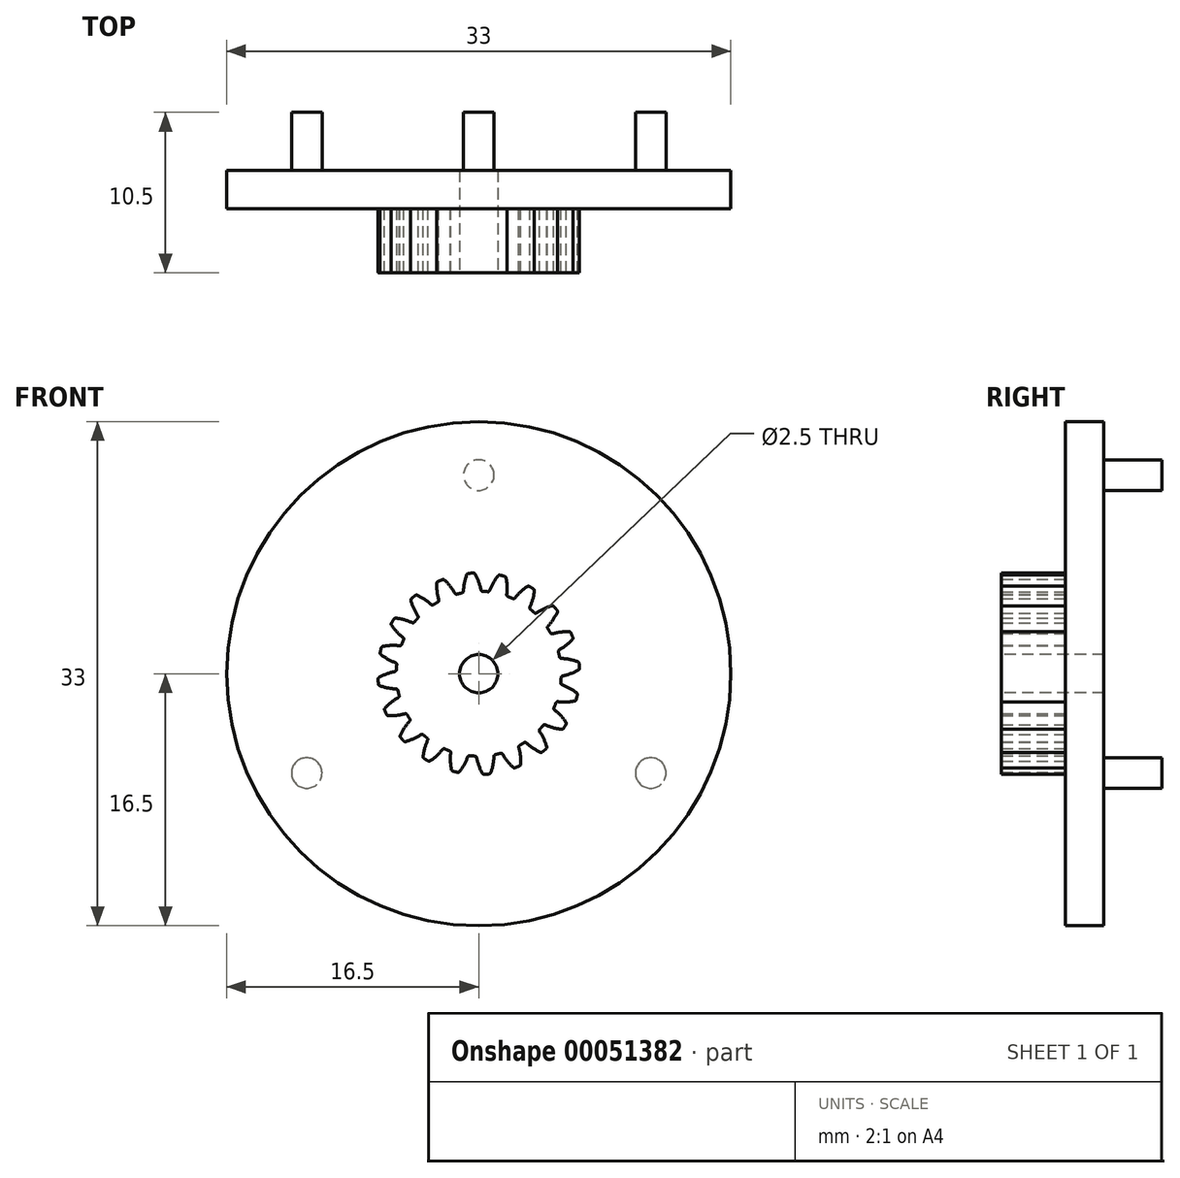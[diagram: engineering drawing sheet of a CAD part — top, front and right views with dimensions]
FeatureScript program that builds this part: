
annotation { "Feature Type Name" : "Feature", "Feature Type Description" : "" }
export const myFeature = defineFeature(function(context is Context, id is Id, definition is map)
    precondition{}
    {
        {
            var Q0;
            Q0=qCreatedBy(makeId("Front.planeOp"),FACE);
            var sketch = newSketch(context, id + "F0", { "sketchPlane" : qUnion([Q0])});
            skCircle(sketch, "E0", {"center": v(0, 0) * mm, "radius": 6 * mm, "construction": true});
            skCircle(sketch, "E1", {"center": v(0, 0) * mm, "radius": 5.4 * mm, "construction": true});
            skCircle(sketch, "E2", {"center": v(0, 0) * mm, "radius": 6.6 * mm, "construction": true});
            skLineSegment(sketch, "E3", {"start": v(0, 0) * mm, "end": v(0, 7.77) * mm, "construction": true});
            skPoint(sketch, "E4", {"position": v(0, 6) * mm});
            skLineSegment(sketch, "E5", {"start": v(0, 6) * mm, "end": v(-7.8, 6) * mm, "construction": true});
            skCircle(sketch, "E6.cCircle", {"center": v(0, 0) * mm, "radius": 7.77 * mm, "construction": true});
            skLineSegment(sketch, "E6.0", {"start": v(-0.61, 7.77) * mm, "end": v(0.61, 7.77) * mm, "construction": true});
            skLineSegment(sketch, "E6.1", {"start": v(0.61, 7.77) * mm, "end": v(1.82, 7.58) * mm, "construction": true});
            skLineSegment(sketch, "E6.2", {"start": v(1.82, 7.58) * mm, "end": v(2.98, 7.2) * mm, "construction": true});
            skLineSegment(sketch, "E6.3", {"start": v(2.98, 7.2) * mm, "end": v(4.07, 6.65) * mm, "construction": true});
            skLineSegment(sketch, "E6.4", {"start": v(4.07, 6.65) * mm, "end": v(5.06, 5.93) * mm, "construction": true});
            skLineSegment(sketch, "E6.5", {"start": v(5.06, 5.93) * mm, "end": v(5.93, 5.06) * mm, "construction": true});
            skLineSegment(sketch, "E6.6", {"start": v(5.93, 5.06) * mm, "end": v(6.65, 4.07) * mm, "construction": true});
            skLineSegment(sketch, "E6.7", {"start": v(6.65, 4.07) * mm, "end": v(7.2, 2.98) * mm, "construction": true});
            skLineSegment(sketch, "E6.8", {"start": v(7.2, 2.98) * mm, "end": v(7.58, 1.82) * mm, "construction": true});
            skLineSegment(sketch, "E6.9", {"start": v(7.58, 1.82) * mm, "end": v(7.77, 0.61) * mm, "construction": true});
            skLineSegment(sketch, "E6.10", {"start": v(7.77, 0.61) * mm, "end": v(7.77, -0.61) * mm, "construction": true});
            skLineSegment(sketch, "E6.11", {"start": v(7.77, -0.61) * mm, "end": v(7.58, -1.82) * mm, "construction": true});
            skLineSegment(sketch, "E6.12", {"start": v(7.58, -1.82) * mm, "end": v(7.2, -2.98) * mm, "construction": true});
            skLineSegment(sketch, "E6.13", {"start": v(7.2, -2.98) * mm, "end": v(6.65, -4.07) * mm, "construction": true});
            skLineSegment(sketch, "E6.14", {"start": v(6.65, -4.07) * mm, "end": v(5.93, -5.06) * mm, "construction": true});
            skLineSegment(sketch, "E6.15", {"start": v(5.93, -5.06) * mm, "end": v(5.06, -5.93) * mm, "construction": true});
            skLineSegment(sketch, "E6.16", {"start": v(5.06, -5.93) * mm, "end": v(4.07, -6.65) * mm, "construction": true});
            skLineSegment(sketch, "E6.17", {"start": v(4.07, -6.65) * mm, "end": v(2.98, -7.2) * mm, "construction": true});
            skLineSegment(sketch, "E6.18", {"start": v(2.98, -7.2) * mm, "end": v(1.82, -7.58) * mm, "construction": true});
            skLineSegment(sketch, "E6.19", {"start": v(1.82, -7.58) * mm, "end": v(0.61, -7.77) * mm, "construction": true});
            skLineSegment(sketch, "E6.20", {"start": v(0.61, -7.77) * mm, "end": v(-0.61, -7.77) * mm, "construction": true});
            skLineSegment(sketch, "E6.21", {"start": v(-0.61, -7.77) * mm, "end": v(-1.82, -7.58) * mm, "construction": true});
            skLineSegment(sketch, "E6.22", {"start": v(-1.82, -7.58) * mm, "end": v(-2.98, -7.2) * mm, "construction": true});
            skLineSegment(sketch, "E6.23", {"start": v(-2.98, -7.2) * mm, "end": v(-4.07, -6.65) * mm, "construction": true});
            skLineSegment(sketch, "E6.24", {"start": v(-4.07, -6.65) * mm, "end": v(-5.06, -5.93) * mm, "construction": true});
            skLineSegment(sketch, "E6.25", {"start": v(-5.06, -5.93) * mm, "end": v(-5.93, -5.06) * mm, "construction": true});
            skLineSegment(sketch, "E6.26", {"start": v(-5.93, -5.06) * mm, "end": v(-6.65, -4.07) * mm, "construction": true});
            skLineSegment(sketch, "E6.27", {"start": v(-6.65, -4.07) * mm, "end": v(-7.2, -2.98) * mm, "construction": true});
            skLineSegment(sketch, "E6.28", {"start": v(-7.2, -2.98) * mm, "end": v(-7.58, -1.82) * mm, "construction": true});
            skLineSegment(sketch, "E6.29", {"start": v(-7.58, -1.82) * mm, "end": v(-7.77, -0.61) * mm, "construction": true});
            skLineSegment(sketch, "E6.30", {"start": v(-7.77, -0.61) * mm, "end": v(-7.77, 0.61) * mm, "construction": true});
            skLineSegment(sketch, "E6.31", {"start": v(-7.77, 0.61) * mm, "end": v(-7.58, 1.82) * mm, "construction": true});
            skLineSegment(sketch, "E6.32", {"start": v(-7.58, 1.82) * mm, "end": v(-7.2, 2.98) * mm, "construction": true});
            skLineSegment(sketch, "E6.33", {"start": v(-7.2, 2.98) * mm, "end": v(-6.65, 4.07) * mm, "construction": true});
            skLineSegment(sketch, "E6.34", {"start": v(-6.65, 4.07) * mm, "end": v(-5.93, 5.06) * mm, "construction": true});
            skLineSegment(sketch, "E6.35", {"start": v(-5.93, 5.06) * mm, "end": v(-5.06, 5.93) * mm, "construction": true});
            skLineSegment(sketch, "E6.36", {"start": v(-5.06, 5.93) * mm, "end": v(-4.07, 6.65) * mm, "construction": true});
            skLineSegment(sketch, "E6.37", {"start": v(-4.07, 6.65) * mm, "end": v(-2.98, 7.2) * mm, "construction": true});
            skLineSegment(sketch, "E6.38", {"start": v(-2.98, 7.2) * mm, "end": v(-1.82, 7.58) * mm, "construction": true});
            skLineSegment(sketch, "E6.39", {"start": v(-1.82, 7.58) * mm, "end": v(-0.61, 7.77) * mm, "construction": true});
            skPoint(sketch, "E6.0.midPoint", {"position": v(0, 7.77) * mm});
            skLineSegment(sketch, "E7.0", {"start": v(0, 7.77) * mm, "end": v(1.22, 7.68) * mm, "construction": true});
            skLineSegment(sketch, "E7.1", {"start": v(1.22, 7.68) * mm, "end": v(2.4, 7.4) * mm, "construction": true});
            skLineSegment(sketch, "E7.2", {"start": v(2.4, 7.4) * mm, "end": v(3.53, 6.93) * mm, "construction": true});
            skLineSegment(sketch, "E7.3", {"start": v(3.53, 6.93) * mm, "end": v(4.57, 6.29) * mm, "construction": true});
            skLineSegment(sketch, "E7.4", {"start": v(4.57, 6.29) * mm, "end": v(5.5, 5.5) * mm, "construction": true});
            skLineSegment(sketch, "E7.5", {"start": v(5.5, 5.5) * mm, "end": v(6.29, 4.57) * mm, "construction": true});
            skLineSegment(sketch, "E7.6", {"start": v(6.29, 4.57) * mm, "end": v(6.93, 3.53) * mm, "construction": true});
            skLineSegment(sketch, "E7.7", {"start": v(6.93, 3.53) * mm, "end": v(7.4, 2.4) * mm, "construction": true});
            skLineSegment(sketch, "E7.8", {"start": v(7.4, 2.4) * mm, "end": v(7.68, 1.22) * mm, "construction": true});
            skLineSegment(sketch, "E7.9", {"start": v(7.68, 1.22) * mm, "end": v(7.77, 0) * mm, "construction": true});
            skLineSegment(sketch, "E7.10", {"start": v(7.77, 0) * mm, "end": v(7.68, -1.22) * mm, "construction": true});
            skLineSegment(sketch, "E7.11", {"start": v(7.68, -1.22) * mm, "end": v(7.4, -2.4) * mm, "construction": true});
            skLineSegment(sketch, "E7.12", {"start": v(7.4, -2.4) * mm, "end": v(6.93, -3.53) * mm, "construction": true});
            skLineSegment(sketch, "E7.13", {"start": v(6.93, -3.53) * mm, "end": v(6.29, -4.57) * mm, "construction": true});
            skLineSegment(sketch, "E7.14", {"start": v(6.29, -4.57) * mm, "end": v(5.5, -5.5) * mm, "construction": true});
            skLineSegment(sketch, "E7.15", {"start": v(5.5, -5.5) * mm, "end": v(4.57, -6.29) * mm, "construction": true});
            skLineSegment(sketch, "E7.16", {"start": v(4.57, -6.29) * mm, "end": v(3.53, -6.93) * mm, "construction": true});
            skLineSegment(sketch, "E7.17", {"start": v(3.53, -6.93) * mm, "end": v(2.4, -7.4) * mm, "construction": true});
            skLineSegment(sketch, "E7.18", {"start": v(2.4, -7.4) * mm, "end": v(1.22, -7.68) * mm, "construction": true});
            skLineSegment(sketch, "E7.19", {"start": v(1.22, -7.68) * mm, "end": v(0, -7.77) * mm, "construction": true});
            skLineSegment(sketch, "E7.20", {"start": v(0, -7.77) * mm, "end": v(-1.22, -7.68) * mm, "construction": true});
            skLineSegment(sketch, "E7.21", {"start": v(-1.22, -7.68) * mm, "end": v(-2.4, -7.4) * mm, "construction": true});
            skLineSegment(sketch, "E7.22", {"start": v(-2.4, -7.4) * mm, "end": v(-3.53, -6.93) * mm, "construction": true});
            skLineSegment(sketch, "E7.23", {"start": v(-3.53, -6.93) * mm, "end": v(-4.57, -6.29) * mm, "construction": true});
            skLineSegment(sketch, "E7.24", {"start": v(-4.57, -6.29) * mm, "end": v(-5.5, -5.5) * mm, "construction": true});
            skLineSegment(sketch, "E7.25", {"start": v(-5.5, -5.5) * mm, "end": v(-6.29, -4.57) * mm, "construction": true});
            skLineSegment(sketch, "E7.26", {"start": v(-6.29, -4.57) * mm, "end": v(-6.93, -3.53) * mm, "construction": true});
            skLineSegment(sketch, "E7.27", {"start": v(-6.93, -3.53) * mm, "end": v(-7.4, -2.4) * mm, "construction": true});
            skLineSegment(sketch, "E7.28", {"start": v(-7.4, -2.4) * mm, "end": v(-7.68, -1.22) * mm, "construction": true});
            skLineSegment(sketch, "E7.29", {"start": v(-7.68, -1.22) * mm, "end": v(-7.77, 0) * mm, "construction": true});
            skLineSegment(sketch, "E7.30", {"start": v(-7.77, 0) * mm, "end": v(-7.68, 1.22) * mm, "construction": true});
            skLineSegment(sketch, "E7.31", {"start": v(-7.68, 1.22) * mm, "end": v(-7.4, 2.4) * mm, "construction": true});
            skLineSegment(sketch, "E7.32", {"start": v(-7.4, 2.4) * mm, "end": v(-6.93, 3.53) * mm, "construction": true});
            skLineSegment(sketch, "E7.33", {"start": v(-6.93, 3.53) * mm, "end": v(-6.29, 4.57) * mm, "construction": true});
            skLineSegment(sketch, "E7.34", {"start": v(-6.29, 4.57) * mm, "end": v(-5.5, 5.5) * mm, "construction": true});
            skLineSegment(sketch, "E7.35", {"start": v(-5.5, 5.5) * mm, "end": v(-4.57, 6.29) * mm, "construction": true});
            skLineSegment(sketch, "E7.36", {"start": v(-4.57, 6.29) * mm, "end": v(-3.53, 6.93) * mm, "construction": true});
            skLineSegment(sketch, "E7.37", {"start": v(-3.53, 6.93) * mm, "end": v(-2.4, 7.4) * mm, "construction": true});
            skLineSegment(sketch, "E7.38", {"start": v(-2.4, 7.4) * mm, "end": v(-1.22, 7.68) * mm, "construction": true});
            skLineSegment(sketch, "E7.39", {"start": v(-1.22, 7.68) * mm, "end": v(0, 7.77) * mm, "construction": true});
            skLineSegment(sketch, "E8", {"start": v(0, 0) * mm, "end": v(-0.61, 7.77) * mm, "construction": true});
            skLineSegment(sketch, "E9", {"start": v(0, 6) * mm, "end": v(-7.35, 3.32) * mm, "construction": true});
            skCircle(sketch, "E10", {"center": v(0, 6) * mm, "radius": 3.6 * mm, "construction": true});
            skPoint(sketch, "E11", {"position": v(-3.38, 4.77) * mm});
            skCircle(sketch, "E12", {"center": v(-3.38, 4.77) * mm, "radius": 3.6 * mm, "construction": true});
            skArc(sketch, "E13", {"start": v(-0.24, 6.53) * mm, "mid": v(0, 6.02) * mm, "end": v(0.14, 5.49) * mm});
            skArc(sketch, "E14.MirrorCS", {"start": v(-0.78, 6.49) * mm, "mid": v(-0.93, 5.95) * mm, "end": v(-1, 5.4) * mm});
            skArc(sketch, "E15", {"start": v(-0.68, 6.56) * mm, "mid": v(-0.52, 6.58) * mm, "end": v(-0.35, 6.6) * mm});
            skArc(sketch, "E16", {"start": v(-1.1, 5.29) * mm, "mid": v(0.42, -5.38) * mm, "end": v(0.26, 5.4) * mm});
            skPoint(sketch, "E17.visualSharp", {"position": v(-1, 5.3) * mm});
            skArc(sketch, "E17.filletArc", {"start": v(-1.1, 5.29) * mm, "mid": v(-1.03, 5.33) * mm, "end": v(-1, 5.4) * mm});
            skPoint(sketch, "E18.visualSharp", {"position": v(0.16, 5.4) * mm});
            skArc(sketch, "E18.filletArc", {"start": v(0.14, 5.49) * mm, "mid": v(0.18, 5.42) * mm, "end": v(0.26, 5.4) * mm});
            skPoint(sketch, "E19.visualSharp", {"position": v(-0.76, 6.56) * mm});
            skArc(sketch, "E19.filletArc", {"start": v(-0.68, 6.56) * mm, "mid": v(-0.74, 6.54) * mm, "end": v(-0.78, 6.49) * mm});
            skPoint(sketch, "E20.visualSharp", {"position": v(-0.28, 6.6) * mm});
            skArc(sketch, "E20.filletArc", {"start": v(-0.24, 6.53) * mm, "mid": v(-0.29, 6.58) * mm, "end": v(-0.35, 6.6) * mm});
            skLineSegment(sketch, "E21", {"start": v(0, 0) * mm, "end": v(-1.44, 6.92) * mm, "construction": true});
            skPoint(sketch, "E22.1.0", {"position": v(-1.51, 5.18) * mm});
            skPoint(sketch, "E22.1.1", {"position": v(-1.85, 5.7) * mm});
            skArc(sketch, "E22.1.2", {"start": v(-2.25, 6.13) * mm, "mid": v(-1.87, 5.73) * mm, "end": v(-1.56, 5.27) * mm});
            skArc(sketch, "E22.1.3", {"start": v(-2.68, 6.03) * mm, "mid": v(-2.53, 6.1) * mm, "end": v(-2.37, 6.16) * mm});
            skPoint(sketch, "E22.1.4", {"position": v(-2.3, 6.18) * mm});
            skPoint(sketch, "E22.1.5", {"position": v(-2.6, 4.74) * mm});
            skArc(sketch, "E22.1.6", {"start": v(-2.75, 5.93) * mm, "mid": v(-2.73, 5.37) * mm, "end": v(-2.62, 4.83) * mm});
            skPoint(sketch, "E22.1.7", {"position": v(-2.74, 6) * mm});
            skArc(sketch, "E22.1.8", {"start": v(-1.56, 5.27) * mm, "mid": v(-1.5, 5.21) * mm, "end": v(-1.42, 5.2) * mm});
            skArc(sketch, "E22.1.9", {"start": v(-2.68, 6.03) * mm, "mid": v(-2.73, 6) * mm, "end": v(-2.75, 5.93) * mm});
            skArc(sketch, "E22.1.10", {"start": v(-2.68, 4.69) * mm, "mid": v(-2.63, 4.75) * mm, "end": v(-2.62, 4.83) * mm});
            skArc(sketch, "E22.1.11", {"start": v(-2.25, 6.13) * mm, "mid": v(-2.3, 6.16) * mm, "end": v(-2.37, 6.16) * mm});
            skPoint(sketch, "E22.2.0", {"position": v(-3.04, 4.46) * mm});
            skPoint(sketch, "E22.2.1", {"position": v(-3.53, 4.85) * mm});
            skArc(sketch, "E22.2.2", {"start": v(-4.03, 5.14) * mm, "mid": v(-3.55, 4.87) * mm, "end": v(-3.11, 4.53) * mm});
            skArc(sketch, "E22.2.3", {"start": v(-4.4, 4.91) * mm, "mid": v(-4.29, 5.02) * mm, "end": v(-4.16, 5.12) * mm});
            skPoint(sketch, "E22.2.4", {"position": v(-4.1, 5.17) * mm});
            skPoint(sketch, "E22.2.5", {"position": v(-3.93, 3.7) * mm});
            skArc(sketch, "E22.2.6", {"start": v(-4.45, 4.79) * mm, "mid": v(-4.25, 4.27) * mm, "end": v(-3.98, 3.78) * mm});
            skPoint(sketch, "E22.2.7", {"position": v(-4.46, 4.86) * mm});
            skArc(sketch, "E22.2.8", {"start": v(-3.11, 4.53) * mm, "mid": v(-3.04, 4.5) * mm, "end": v(-2.96, 4.51) * mm});
            skArc(sketch, "E22.2.9", {"start": v(-4.4, 4.91) * mm, "mid": v(-4.45, 4.85) * mm, "end": v(-4.45, 4.79) * mm});
            skArc(sketch, "E22.2.10", {"start": v(-4, 3.63) * mm, "mid": v(-3.96, 3.7) * mm, "end": v(-3.98, 3.78) * mm});
            skArc(sketch, "E22.2.11", {"start": v(-4.03, 5.14) * mm, "mid": v(-4.1, 5.15) * mm, "end": v(-4.16, 5.12) * mm});
            skPoint(sketch, "E22.3.0", {"position": v(-4.27, 3.3) * mm});
            skPoint(sketch, "E22.3.1", {"position": v(-4.85, 3.53) * mm});
            skArc(sketch, "E22.3.2", {"start": v(-5.43, 3.64) * mm, "mid": v(-4.88, 3.53) * mm, "end": v(-4.36, 3.34) * mm});
            skArc(sketch, "E22.3.3", {"start": v(-5.71, 3.3) * mm, "mid": v(-5.63, 3.45) * mm, "end": v(-5.54, 3.59) * mm});
            skPoint(sketch, "E22.3.4", {"position": v(-5.5, 3.65) * mm});
            skPoint(sketch, "E22.3.5", {"position": v(-4.88, 2.3) * mm});
            skArc(sketch, "E22.3.6", {"start": v(-5.7, 3.18) * mm, "mid": v(-5.36, 2.74) * mm, "end": v(-4.96, 2.36) * mm});
            skPoint(sketch, "E22.3.7", {"position": v(-5.75, 3.24) * mm});
            skArc(sketch, "E22.3.8", {"start": v(-4.36, 3.34) * mm, "mid": v(-4.28, 3.34) * mm, "end": v(-4.21, 3.38) * mm});
            skArc(sketch, "E22.3.9", {"start": v(-5.71, 3.3) * mm, "mid": v(-5.73, 3.24) * mm, "end": v(-5.7, 3.18) * mm});
            skArc(sketch, "E22.3.10", {"start": v(-4.92, 2.22) * mm, "mid": v(-4.92, 2.3) * mm, "end": v(-4.96, 2.36) * mm});
            skArc(sketch, "E22.3.11", {"start": v(-5.43, 3.64) * mm, "mid": v(-5.5, 3.63) * mm, "end": v(-5.54, 3.59) * mm});
            skPoint(sketch, "E22.4.0", {"position": v(-5.08, 1.82) * mm});
            skPoint(sketch, "E22.4.1", {"position": v(-5.7, 1.85) * mm});
            skArc(sketch, "E22.4.2", {"start": v(-6.28, 1.79) * mm, "mid": v(-5.73, 1.85) * mm, "end": v(-5.18, 1.83) * mm});
            skArc(sketch, "E22.4.3", {"start": v(-6.45, 1.38) * mm, "mid": v(-6.42, 1.54) * mm, "end": v(-6.38, 1.7) * mm});
            skPoint(sketch, "E22.4.4", {"position": v(-6.36, 1.77) * mm});
            skPoint(sketch, "E22.4.5", {"position": v(-5.36, 0.68) * mm});
            skArc(sketch, "E22.4.6", {"start": v(-6.41, 1.26) * mm, "mid": v(-5.95, 0.95) * mm, "end": v(-5.44, 0.72) * mm});
            skPoint(sketch, "E22.4.7", {"position": v(-6.47, 1.3) * mm});
            skArc(sketch, "E22.4.8", {"start": v(-5.18, 1.83) * mm, "mid": v(-5.1, 1.85) * mm, "end": v(-5.05, 1.91) * mm});
            skArc(sketch, "E22.4.9", {"start": v(-6.45, 1.38) * mm, "mid": v(-6.45, 1.31) * mm, "end": v(-6.41, 1.26) * mm});
            skArc(sketch, "E22.4.10", {"start": v(-5.37, 0.6) * mm, "mid": v(-5.38, 0.67) * mm, "end": v(-5.44, 0.72) * mm});
            skArc(sketch, "E22.4.11", {"start": v(-6.28, 1.79) * mm, "mid": v(-6.34, 1.76) * mm, "end": v(-6.38, 1.7) * mm});
            skPoint(sketch, "E22.5.0", {"position": v(-5.4, 0.16) * mm});
            skPoint(sketch, "E22.5.1", {"position": v(-6, 0) * mm});
            skArc(sketch, "E22.5.2", {"start": v(-6.53, -0.24) * mm, "mid": v(-6.02, 0) * mm, "end": v(-5.49, 0.14) * mm});
            skArc(sketch, "E22.5.3", {"start": v(-6.56, -0.68) * mm, "mid": v(-6.58, -0.52) * mm, "end": v(-6.6, -0.35) * mm});
            skPoint(sketch, "E22.5.4", {"position": v(-6.6, -0.28) * mm});
            skPoint(sketch, "E22.5.5", {"position": v(-5.3, -1) * mm});
            skArc(sketch, "E22.5.6", {"start": v(-6.49, -0.78) * mm, "mid": v(-5.95, -0.93) * mm, "end": v(-5.4, -1) * mm});
            skPoint(sketch, "E22.5.7", {"position": v(-6.56, -0.76) * mm});
            skArc(sketch, "E22.5.8", {"start": v(-5.49, 0.14) * mm, "mid": v(-5.42, 0.18) * mm, "end": v(-5.4, 0.26) * mm});
            skArc(sketch, "E22.5.9", {"start": v(-6.56, -0.68) * mm, "mid": v(-6.54, -0.74) * mm, "end": v(-6.49, -0.78) * mm});
            skArc(sketch, "E22.5.10", {"start": v(-5.29, -1.1) * mm, "mid": v(-5.33, -1.03) * mm, "end": v(-5.4, -1) * mm});
            skArc(sketch, "E22.5.11", {"start": v(-6.53, -0.24) * mm, "mid": v(-6.58, -0.29) * mm, "end": v(-6.6, -0.35) * mm});
            skPoint(sketch, "E22.6.0", {"position": v(-5.18, -1.51) * mm});
            skPoint(sketch, "E22.6.1", {"position": v(-5.7, -1.85) * mm});
            skArc(sketch, "E22.6.2", {"start": v(-6.13, -2.25) * mm, "mid": v(-5.73, -1.87) * mm, "end": v(-5.27, -1.56) * mm});
            skArc(sketch, "E22.6.3", {"start": v(-6.03, -2.68) * mm, "mid": v(-6.1, -2.53) * mm, "end": v(-6.16, -2.37) * mm});
            skPoint(sketch, "E22.6.4", {"position": v(-6.18, -2.3) * mm});
            skPoint(sketch, "E22.6.5", {"position": v(-4.74, -2.6) * mm});
            skArc(sketch, "E22.6.6", {"start": v(-5.93, -2.75) * mm, "mid": v(-5.37, -2.73) * mm, "end": v(-4.83, -2.62) * mm});
            skPoint(sketch, "E22.6.7", {"position": v(-6, -2.74) * mm});
            skArc(sketch, "E22.6.8", {"start": v(-5.27, -1.56) * mm, "mid": v(-5.21, -1.5) * mm, "end": v(-5.2, -1.42) * mm});
            skArc(sketch, "E22.6.9", {"start": v(-6.03, -2.68) * mm, "mid": v(-6, -2.73) * mm, "end": v(-5.93, -2.75) * mm});
            skArc(sketch, "E22.6.10", {"start": v(-4.69, -2.68) * mm, "mid": v(-4.75, -2.63) * mm, "end": v(-4.83, -2.62) * mm});
            skArc(sketch, "E22.6.11", {"start": v(-6.13, -2.25) * mm, "mid": v(-6.16, -2.3) * mm, "end": v(-6.16, -2.37) * mm});
            skPoint(sketch, "E22.7.0", {"position": v(-4.46, -3.04) * mm});
            skPoint(sketch, "E22.7.1", {"position": v(-4.85, -3.53) * mm});
            skArc(sketch, "E22.7.2", {"start": v(-5.14, -4.03) * mm, "mid": v(-4.87, -3.55) * mm, "end": v(-4.53, -3.11) * mm});
            skArc(sketch, "E22.7.3", {"start": v(-4.91, -4.4) * mm, "mid": v(-5.02, -4.29) * mm, "end": v(-5.12, -4.16) * mm});
            skPoint(sketch, "E22.7.4", {"position": v(-5.17, -4.1) * mm});
            skPoint(sketch, "E22.7.5", {"position": v(-3.7, -3.93) * mm});
            skArc(sketch, "E22.7.6", {"start": v(-4.79, -4.45) * mm, "mid": v(-4.27, -4.25) * mm, "end": v(-3.78, -3.98) * mm});
            skPoint(sketch, "E22.7.7", {"position": v(-4.86, -4.46) * mm});
            skArc(sketch, "E22.7.8", {"start": v(-4.53, -3.11) * mm, "mid": v(-4.5, -3.04) * mm, "end": v(-4.51, -2.96) * mm});
            skArc(sketch, "E22.7.9", {"start": v(-4.91, -4.4) * mm, "mid": v(-4.85, -4.45) * mm, "end": v(-4.79, -4.45) * mm});
            skArc(sketch, "E22.7.10", {"start": v(-3.63, -4) * mm, "mid": v(-3.7, -3.96) * mm, "end": v(-3.78, -3.98) * mm});
            skArc(sketch, "E22.7.11", {"start": v(-5.14, -4.03) * mm, "mid": v(-5.15, -4.1) * mm, "end": v(-5.12, -4.16) * mm});
            skPoint(sketch, "E22.8.0", {"position": v(-3.3, -4.27) * mm});
            skPoint(sketch, "E22.8.1", {"position": v(-3.53, -4.85) * mm});
            skArc(sketch, "E22.8.2", {"start": v(-3.64, -5.43) * mm, "mid": v(-3.53, -4.88) * mm, "end": v(-3.34, -4.36) * mm});
            skArc(sketch, "E22.8.3", {"start": v(-3.3, -5.71) * mm, "mid": v(-3.45, -5.63) * mm, "end": v(-3.59, -5.54) * mm});
            skPoint(sketch, "E22.8.4", {"position": v(-3.65, -5.5) * mm});
            skPoint(sketch, "E22.8.5", {"position": v(-2.3, -4.88) * mm});
            skArc(sketch, "E22.8.6", {"start": v(-3.18, -5.7) * mm, "mid": v(-2.74, -5.36) * mm, "end": v(-2.36, -4.96) * mm});
            skPoint(sketch, "E22.8.7", {"position": v(-3.24, -5.75) * mm});
            skArc(sketch, "E22.8.8", {"start": v(-3.34, -4.36) * mm, "mid": v(-3.34, -4.28) * mm, "end": v(-3.38, -4.21) * mm});
            skArc(sketch, "E22.8.9", {"start": v(-3.3, -5.71) * mm, "mid": v(-3.24, -5.73) * mm, "end": v(-3.18, -5.7) * mm});
            skArc(sketch, "E22.8.10", {"start": v(-2.22, -4.92) * mm, "mid": v(-2.3, -4.92) * mm, "end": v(-2.36, -4.96) * mm});
            skArc(sketch, "E22.8.11", {"start": v(-3.64, -5.43) * mm, "mid": v(-3.63, -5.5) * mm, "end": v(-3.59, -5.54) * mm});
            skPoint(sketch, "E22.9.0", {"position": v(-1.82, -5.08) * mm});
            skPoint(sketch, "E22.9.1", {"position": v(-1.85, -5.7) * mm});
            skArc(sketch, "E22.9.2", {"start": v(-1.79, -6.28) * mm, "mid": v(-1.85, -5.73) * mm, "end": v(-1.83, -5.18) * mm});
            skArc(sketch, "E22.9.3", {"start": v(-1.38, -6.45) * mm, "mid": v(-1.54, -6.42) * mm, "end": v(-1.7, -6.38) * mm});
            skPoint(sketch, "E22.9.4", {"position": v(-1.77, -6.36) * mm});
            skPoint(sketch, "E22.9.5", {"position": v(-0.68, -5.36) * mm});
            skArc(sketch, "E22.9.6", {"start": v(-1.26, -6.41) * mm, "mid": v(-0.95, -5.95) * mm, "end": v(-0.72, -5.44) * mm});
            skPoint(sketch, "E22.9.7", {"position": v(-1.3, -6.47) * mm});
            skArc(sketch, "E22.9.8", {"start": v(-1.83, -5.18) * mm, "mid": v(-1.85, -5.1) * mm, "end": v(-1.91, -5.05) * mm});
            skArc(sketch, "E22.9.9", {"start": v(-1.38, -6.45) * mm, "mid": v(-1.31, -6.45) * mm, "end": v(-1.26, -6.41) * mm});
            skArc(sketch, "E22.9.10", {"start": v(-0.6, -5.37) * mm, "mid": v(-0.67, -5.38) * mm, "end": v(-0.72, -5.44) * mm});
            skArc(sketch, "E22.9.11", {"start": v(-1.79, -6.28) * mm, "mid": v(-1.76, -6.34) * mm, "end": v(-1.7, -6.38) * mm});
            skPoint(sketch, "E22.10.0", {"position": v(-0.16, -5.4) * mm});
            skPoint(sketch, "E22.10.1", {"position": v(0, -6) * mm});
            skArc(sketch, "E22.10.2", {"start": v(0.24, -6.53) * mm, "mid": v(0, -6.02) * mm, "end": v(-0.14, -5.49) * mm});
            skArc(sketch, "E22.10.3", {"start": v(0.68, -6.56) * mm, "mid": v(0.52, -6.58) * mm, "end": v(0.35, -6.6) * mm});
            skPoint(sketch, "E22.10.4", {"position": v(0.28, -6.6) * mm});
            skPoint(sketch, "E22.10.5", {"position": v(1, -5.3) * mm});
            skArc(sketch, "E22.10.6", {"start": v(0.78, -6.49) * mm, "mid": v(0.93, -5.95) * mm, "end": v(1, -5.4) * mm});
            skPoint(sketch, "E22.10.7", {"position": v(0.76, -6.56) * mm});
            skArc(sketch, "E22.10.8", {"start": v(-0.14, -5.49) * mm, "mid": v(-0.18, -5.42) * mm, "end": v(-0.26, -5.4) * mm});
            skArc(sketch, "E22.10.9", {"start": v(0.68, -6.56) * mm, "mid": v(0.74, -6.54) * mm, "end": v(0.78, -6.49) * mm});
            skArc(sketch, "E22.10.10", {"start": v(1.1, -5.29) * mm, "mid": v(1.03, -5.33) * mm, "end": v(1, -5.4) * mm});
            skArc(sketch, "E22.10.11", {"start": v(0.24, -6.53) * mm, "mid": v(0.29, -6.58) * mm, "end": v(0.35, -6.6) * mm});
            skPoint(sketch, "E22.11.0", {"position": v(1.51, -5.18) * mm});
            skPoint(sketch, "E22.11.1", {"position": v(1.85, -5.7) * mm});
            skArc(sketch, "E22.11.2", {"start": v(2.25, -6.13) * mm, "mid": v(1.87, -5.73) * mm, "end": v(1.56, -5.27) * mm});
            skArc(sketch, "E22.11.3", {"start": v(2.68, -6.03) * mm, "mid": v(2.53, -6.1) * mm, "end": v(2.37, -6.16) * mm});
            skPoint(sketch, "E22.11.4", {"position": v(2.3, -6.18) * mm});
            skPoint(sketch, "E22.11.5", {"position": v(2.6, -4.74) * mm});
            skArc(sketch, "E22.11.6", {"start": v(2.75, -5.93) * mm, "mid": v(2.73, -5.37) * mm, "end": v(2.62, -4.83) * mm});
            skPoint(sketch, "E22.11.7", {"position": v(2.74, -6) * mm});
            skArc(sketch, "E22.11.8", {"start": v(1.56, -5.27) * mm, "mid": v(1.5, -5.21) * mm, "end": v(1.42, -5.2) * mm});
            skArc(sketch, "E22.11.9", {"start": v(2.68, -6.03) * mm, "mid": v(2.73, -6) * mm, "end": v(2.75, -5.93) * mm});
            skArc(sketch, "E22.11.10", {"start": v(2.68, -4.69) * mm, "mid": v(2.63, -4.75) * mm, "end": v(2.62, -4.83) * mm});
            skArc(sketch, "E22.11.11", {"start": v(2.25, -6.13) * mm, "mid": v(2.3, -6.16) * mm, "end": v(2.37, -6.16) * mm});
            skPoint(sketch, "E22.12.0", {"position": v(3.04, -4.46) * mm});
            skPoint(sketch, "E22.12.1", {"position": v(3.53, -4.85) * mm});
            skArc(sketch, "E22.12.2", {"start": v(4.03, -5.14) * mm, "mid": v(3.55, -4.87) * mm, "end": v(3.11, -4.53) * mm});
            skArc(sketch, "E22.12.3", {"start": v(4.4, -4.91) * mm, "mid": v(4.29, -5.02) * mm, "end": v(4.16, -5.12) * mm});
            skPoint(sketch, "E22.12.4", {"position": v(4.1, -5.17) * mm});
            skPoint(sketch, "E22.12.5", {"position": v(3.93, -3.7) * mm});
            skArc(sketch, "E22.12.6", {"start": v(4.45, -4.79) * mm, "mid": v(4.25, -4.27) * mm, "end": v(3.98, -3.78) * mm});
            skPoint(sketch, "E22.12.7", {"position": v(4.46, -4.86) * mm});
            skArc(sketch, "E22.12.8", {"start": v(3.11, -4.53) * mm, "mid": v(3.04, -4.5) * mm, "end": v(2.96, -4.51) * mm});
            skArc(sketch, "E22.12.9", {"start": v(4.4, -4.91) * mm, "mid": v(4.45, -4.85) * mm, "end": v(4.45, -4.79) * mm});
            skArc(sketch, "E22.12.10", {"start": v(4, -3.63) * mm, "mid": v(3.96, -3.7) * mm, "end": v(3.98, -3.78) * mm});
            skArc(sketch, "E22.12.11", {"start": v(4.03, -5.14) * mm, "mid": v(4.1, -5.15) * mm, "end": v(4.16, -5.12) * mm});
            skPoint(sketch, "E22.13.0", {"position": v(4.27, -3.3) * mm});
            skPoint(sketch, "E22.13.1", {"position": v(4.85, -3.53) * mm});
            skArc(sketch, "E22.13.2", {"start": v(5.43, -3.64) * mm, "mid": v(4.88, -3.53) * mm, "end": v(4.36, -3.34) * mm});
            skArc(sketch, "E22.13.3", {"start": v(5.71, -3.3) * mm, "mid": v(5.63, -3.45) * mm, "end": v(5.54, -3.59) * mm});
            skPoint(sketch, "E22.13.4", {"position": v(5.5, -3.65) * mm});
            skPoint(sketch, "E22.13.5", {"position": v(4.88, -2.3) * mm});
            skArc(sketch, "E22.13.6", {"start": v(5.7, -3.18) * mm, "mid": v(5.36, -2.74) * mm, "end": v(4.96, -2.36) * mm});
            skPoint(sketch, "E22.13.7", {"position": v(5.75, -3.24) * mm});
            skArc(sketch, "E22.13.8", {"start": v(4.36, -3.34) * mm, "mid": v(4.28, -3.34) * mm, "end": v(4.21, -3.38) * mm});
            skArc(sketch, "E22.13.9", {"start": v(5.71, -3.3) * mm, "mid": v(5.73, -3.24) * mm, "end": v(5.7, -3.18) * mm});
            skArc(sketch, "E22.13.10", {"start": v(4.92, -2.22) * mm, "mid": v(4.92, -2.3) * mm, "end": v(4.96, -2.36) * mm});
            skArc(sketch, "E22.13.11", {"start": v(5.43, -3.64) * mm, "mid": v(5.5, -3.63) * mm, "end": v(5.54, -3.59) * mm});
            skPoint(sketch, "E22.14.0", {"position": v(5.08, -1.82) * mm});
            skPoint(sketch, "E22.14.1", {"position": v(5.7, -1.85) * mm});
            skArc(sketch, "E22.14.2", {"start": v(6.28, -1.79) * mm, "mid": v(5.73, -1.85) * mm, "end": v(5.18, -1.83) * mm});
            skArc(sketch, "E22.14.3", {"start": v(6.45, -1.38) * mm, "mid": v(6.42, -1.54) * mm, "end": v(6.38, -1.7) * mm});
            skPoint(sketch, "E22.14.4", {"position": v(6.36, -1.77) * mm});
            skPoint(sketch, "E22.14.5", {"position": v(5.36, -0.68) * mm});
            skArc(sketch, "E22.14.6", {"start": v(6.41, -1.26) * mm, "mid": v(5.95, -0.95) * mm, "end": v(5.44, -0.72) * mm});
            skPoint(sketch, "E22.14.7", {"position": v(6.47, -1.3) * mm});
            skArc(sketch, "E22.14.8", {"start": v(5.18, -1.83) * mm, "mid": v(5.1, -1.85) * mm, "end": v(5.05, -1.91) * mm});
            skArc(sketch, "E22.14.9", {"start": v(6.45, -1.38) * mm, "mid": v(6.45, -1.31) * mm, "end": v(6.41, -1.26) * mm});
            skArc(sketch, "E22.14.10", {"start": v(5.37, -0.6) * mm, "mid": v(5.38, -0.67) * mm, "end": v(5.44, -0.72) * mm});
            skArc(sketch, "E22.14.11", {"start": v(6.28, -1.79) * mm, "mid": v(6.34, -1.76) * mm, "end": v(6.38, -1.7) * mm});
            skPoint(sketch, "E22.15.0", {"position": v(5.4, -0.16) * mm});
            skPoint(sketch, "E22.15.1", {"position": v(6, 0) * mm});
            skArc(sketch, "E22.15.2", {"start": v(6.53, 0.24) * mm, "mid": v(6.02, 0) * mm, "end": v(5.49, -0.14) * mm});
            skArc(sketch, "E22.15.3", {"start": v(6.56, 0.68) * mm, "mid": v(6.58, 0.52) * mm, "end": v(6.6, 0.35) * mm});
            skPoint(sketch, "E22.15.4", {"position": v(6.6, 0.28) * mm});
            skPoint(sketch, "E22.15.5", {"position": v(5.3, 1) * mm});
            skArc(sketch, "E22.15.6", {"start": v(6.49, 0.78) * mm, "mid": v(5.95, 0.93) * mm, "end": v(5.4, 1) * mm});
            skPoint(sketch, "E22.15.7", {"position": v(6.56, 0.76) * mm});
            skArc(sketch, "E22.15.8", {"start": v(5.49, -0.14) * mm, "mid": v(5.42, -0.18) * mm, "end": v(5.4, -0.26) * mm});
            skArc(sketch, "E22.15.9", {"start": v(6.56, 0.68) * mm, "mid": v(6.54, 0.74) * mm, "end": v(6.49, 0.78) * mm});
            skArc(sketch, "E22.15.10", {"start": v(5.29, 1.1) * mm, "mid": v(5.33, 1.03) * mm, "end": v(5.4, 1) * mm});
            skArc(sketch, "E22.15.11", {"start": v(6.53, 0.24) * mm, "mid": v(6.58, 0.29) * mm, "end": v(6.6, 0.35) * mm});
            skPoint(sketch, "E22.16.0", {"position": v(5.18, 1.51) * mm});
            skPoint(sketch, "E22.16.1", {"position": v(5.7, 1.85) * mm});
            skArc(sketch, "E22.16.2", {"start": v(6.13, 2.25) * mm, "mid": v(5.73, 1.87) * mm, "end": v(5.27, 1.56) * mm});
            skArc(sketch, "E22.16.3", {"start": v(6.03, 2.68) * mm, "mid": v(6.1, 2.53) * mm, "end": v(6.16, 2.37) * mm});
            skPoint(sketch, "E22.16.4", {"position": v(6.18, 2.3) * mm});
            skPoint(sketch, "E22.16.5", {"position": v(4.74, 2.6) * mm});
            skArc(sketch, "E22.16.6", {"start": v(5.93, 2.75) * mm, "mid": v(5.37, 2.73) * mm, "end": v(4.83, 2.62) * mm});
            skPoint(sketch, "E22.16.7", {"position": v(6, 2.74) * mm});
            skArc(sketch, "E22.16.8", {"start": v(5.27, 1.56) * mm, "mid": v(5.21, 1.5) * mm, "end": v(5.2, 1.42) * mm});
            skArc(sketch, "E22.16.9", {"start": v(6.03, 2.68) * mm, "mid": v(6, 2.73) * mm, "end": v(5.93, 2.75) * mm});
            skArc(sketch, "E22.16.10", {"start": v(4.69, 2.68) * mm, "mid": v(4.75, 2.63) * mm, "end": v(4.83, 2.62) * mm});
            skArc(sketch, "E22.16.11", {"start": v(6.13, 2.25) * mm, "mid": v(6.16, 2.3) * mm, "end": v(6.16, 2.37) * mm});
            skPoint(sketch, "E22.17.0", {"position": v(4.46, 3.04) * mm});
            skPoint(sketch, "E22.17.1", {"position": v(4.85, 3.53) * mm});
            skArc(sketch, "E22.17.2", {"start": v(5.14, 4.03) * mm, "mid": v(4.87, 3.55) * mm, "end": v(4.53, 3.11) * mm});
            skArc(sketch, "E22.17.3", {"start": v(4.91, 4.4) * mm, "mid": v(5.02, 4.29) * mm, "end": v(5.12, 4.16) * mm});
            skPoint(sketch, "E22.17.4", {"position": v(5.17, 4.1) * mm});
            skPoint(sketch, "E22.17.5", {"position": v(3.7, 3.93) * mm});
            skArc(sketch, "E22.17.6", {"start": v(4.79, 4.45) * mm, "mid": v(4.27, 4.25) * mm, "end": v(3.78, 3.98) * mm});
            skPoint(sketch, "E22.17.7", {"position": v(4.86, 4.46) * mm});
            skArc(sketch, "E22.17.8", {"start": v(4.53, 3.11) * mm, "mid": v(4.5, 3.04) * mm, "end": v(4.51, 2.96) * mm});
            skArc(sketch, "E22.17.9", {"start": v(4.91, 4.4) * mm, "mid": v(4.85, 4.45) * mm, "end": v(4.79, 4.45) * mm});
            skArc(sketch, "E22.17.10", {"start": v(3.63, 4) * mm, "mid": v(3.7, 3.96) * mm, "end": v(3.78, 3.98) * mm});
            skArc(sketch, "E22.17.11", {"start": v(5.14, 4.03) * mm, "mid": v(5.15, 4.1) * mm, "end": v(5.12, 4.16) * mm});
            skPoint(sketch, "E22.18.0", {"position": v(3.3, 4.27) * mm});
            skPoint(sketch, "E22.18.1", {"position": v(3.53, 4.85) * mm});
            skArc(sketch, "E22.18.2", {"start": v(3.64, 5.43) * mm, "mid": v(3.53, 4.88) * mm, "end": v(3.34, 4.36) * mm});
            skArc(sketch, "E22.18.3", {"start": v(3.3, 5.71) * mm, "mid": v(3.45, 5.63) * mm, "end": v(3.59, 5.54) * mm});
            skPoint(sketch, "E22.18.4", {"position": v(3.65, 5.5) * mm});
            skPoint(sketch, "E22.18.5", {"position": v(2.3, 4.88) * mm});
            skArc(sketch, "E22.18.6", {"start": v(3.18, 5.7) * mm, "mid": v(2.74, 5.36) * mm, "end": v(2.36, 4.96) * mm});
            skPoint(sketch, "E22.18.7", {"position": v(3.24, 5.75) * mm});
            skArc(sketch, "E22.18.8", {"start": v(3.34, 4.36) * mm, "mid": v(3.34, 4.28) * mm, "end": v(3.38, 4.21) * mm});
            skArc(sketch, "E22.18.9", {"start": v(3.3, 5.71) * mm, "mid": v(3.24, 5.73) * mm, "end": v(3.18, 5.7) * mm});
            skArc(sketch, "E22.18.10", {"start": v(2.22, 4.92) * mm, "mid": v(2.3, 4.92) * mm, "end": v(2.36, 4.96) * mm});
            skArc(sketch, "E22.18.11", {"start": v(3.64, 5.43) * mm, "mid": v(3.63, 5.5) * mm, "end": v(3.59, 5.54) * mm});
            skPoint(sketch, "E22.19.0", {"position": v(1.82, 5.08) * mm});
            skPoint(sketch, "E22.19.1", {"position": v(1.85, 5.7) * mm});
            skArc(sketch, "E22.19.2", {"start": v(1.79, 6.28) * mm, "mid": v(1.85, 5.73) * mm, "end": v(1.83, 5.18) * mm});
            skArc(sketch, "E22.19.3", {"start": v(1.38, 6.45) * mm, "mid": v(1.54, 6.42) * mm, "end": v(1.7, 6.38) * mm});
            skPoint(sketch, "E22.19.4", {"position": v(1.77, 6.36) * mm});
            skPoint(sketch, "E22.19.5", {"position": v(0.68, 5.36) * mm});
            skArc(sketch, "E22.19.6", {"start": v(1.26, 6.41) * mm, "mid": v(0.95, 5.95) * mm, "end": v(0.72, 5.44) * mm});
            skPoint(sketch, "E22.19.7", {"position": v(1.3, 6.47) * mm});
            skArc(sketch, "E22.19.8", {"start": v(1.83, 5.18) * mm, "mid": v(1.85, 5.1) * mm, "end": v(1.91, 5.05) * mm});
            skArc(sketch, "E22.19.9", {"start": v(1.38, 6.45) * mm, "mid": v(1.31, 6.45) * mm, "end": v(1.26, 6.41) * mm});
            skArc(sketch, "E22.19.10", {"start": v(0.6, 5.37) * mm, "mid": v(0.67, 5.38) * mm, "end": v(0.72, 5.44) * mm});
            skArc(sketch, "E22.19.11", {"start": v(1.79, 6.28) * mm, "mid": v(1.76, 6.34) * mm, "end": v(1.7, 6.38) * mm});
            skSolve(sketch);
        }
        {
            var Q0;
            Q0 = qSketchRegion(id + "F0", true);
            extrude(context, id + "F1", {"entities" : qUnion([Q0]), "depth" : 4.2 * mm});
        }
        {
            var Q0;
            Q0=qCreatedBy(makeId("Front.planeOp"),FACE);
            var sketch = newSketch(context, id + "F2", { "sketchPlane" : qUnion([Q0])});
            skCircle(sketch, "E23", {"center": v(0, 0) * mm, "radius": 16.5 * mm});
            skSolve(sketch);
        }
        {
            var Q0;
            Q0 = qSketchRegion(id + "F2", true);
            extrude(context, id + "F3", {"entities" : qUnion([Q0]), "operationType" : NewBodyOperationType.ADD, "oppositeDirection" : true, "depth" : 2.5 * mm});
        }
        {
            var Q0;
            Q0=makeQuery(id+"F1.opExtrude","CAP_FACE",FACE,{"disambiguationData":[OSD([sQuery(id+"F0.wireOp",EDGE,"E13"),sQuery(id+"F0.wireOp",EDGE,"E14.MirrorCS"),sQuery(id+"F0.wireOp",EDGE,"E15"),sQuery(id+"F0.wireOp",EDGE,"E16"),sQuery(id+"F0.wireOp",EDGE,"E17.filletArc"),sQuery(id+"F0.wireOp",EDGE,"E18.filletArc"),sQuery(id+"F0.wireOp",EDGE,"E19.filletArc"),sQuery(id+"F0.wireOp",EDGE,"E20.filletArc"),sQuery(id+"F0.wireOp",EDGE,"E22.1.2"),sQuery(id+"F0.wireOp",EDGE,"E22.1.3"),sQuery(id+"F0.wireOp",EDGE,"E22.1.6"),sQuery(id+"F0.wireOp",EDGE,"E22.1.8"),sQuery(id+"F0.wireOp",EDGE,"E22.1.9"),sQuery(id+"F0.wireOp",EDGE,"E22.1.10"),sQuery(id+"F0.wireOp",EDGE,"E22.1.11"),sQuery(id+"F0.wireOp",EDGE,"E22.2.2"),sQuery(id+"F0.wireOp",EDGE,"E22.2.3"),sQuery(id+"F0.wireOp",EDGE,"E22.2.6"),sQuery(id+"F0.wireOp",EDGE,"E22.2.8"),sQuery(id+"F0.wireOp",EDGE,"E22.2.9"),sQuery(id+"F0.wireOp",EDGE,"E22.2.10"),sQuery(id+"F0.wireOp",EDGE,"E22.2.11"),sQuery(id+"F0.wireOp",EDGE,"E22.3.2"),sQuery(id+"F0.wireOp",EDGE,"E22.3.3"),sQuery(id+"F0.wireOp",EDGE,"E22.3.6"),sQuery(id+"F0.wireOp",EDGE,"E22.3.8"),sQuery(id+"F0.wireOp",EDGE,"E22.3.9"),sQuery(id+"F0.wireOp",EDGE,"E22.3.10"),sQuery(id+"F0.wireOp",EDGE,"E22.3.11"),sQuery(id+"F0.wireOp",EDGE,"E22.4.2"),sQuery(id+"F0.wireOp",EDGE,"E22.4.3"),sQuery(id+"F0.wireOp",EDGE,"E22.4.6"),sQuery(id+"F0.wireOp",EDGE,"E22.4.8"),sQuery(id+"F0.wireOp",EDGE,"E22.4.9"),sQuery(id+"F0.wireOp",EDGE,"E22.4.10"),sQuery(id+"F0.wireOp",EDGE,"E22.4.11"),sQuery(id+"F0.wireOp",EDGE,"E22.5.2"),sQuery(id+"F0.wireOp",EDGE,"E22.5.3"),sQuery(id+"F0.wireOp",EDGE,"E22.5.6"),sQuery(id+"F0.wireOp",EDGE,"E22.5.8"),sQuery(id+"F0.wireOp",EDGE,"E22.5.9"),sQuery(id+"F0.wireOp",EDGE,"E22.5.10"),sQuery(id+"F0.wireOp",EDGE,"E22.5.11"),sQuery(id+"F0.wireOp",EDGE,"E22.6.2"),sQuery(id+"F0.wireOp",EDGE,"E22.6.3"),sQuery(id+"F0.wireOp",EDGE,"E22.6.6"),sQuery(id+"F0.wireOp",EDGE,"E22.6.8"),sQuery(id+"F0.wireOp",EDGE,"E22.6.9"),sQuery(id+"F0.wireOp",EDGE,"E22.6.10"),sQuery(id+"F0.wireOp",EDGE,"E22.6.11"),sQuery(id+"F0.wireOp",EDGE,"E22.7.2"),sQuery(id+"F0.wireOp",EDGE,"E22.7.3"),sQuery(id+"F0.wireOp",EDGE,"E22.7.6"),sQuery(id+"F0.wireOp",EDGE,"E22.7.8"),sQuery(id+"F0.wireOp",EDGE,"E22.7.9"),sQuery(id+"F0.wireOp",EDGE,"E22.7.10"),sQuery(id+"F0.wireOp",EDGE,"E22.7.11"),sQuery(id+"F0.wireOp",EDGE,"E22.8.2"),sQuery(id+"F0.wireOp",EDGE,"E22.8.3"),sQuery(id+"F0.wireOp",EDGE,"E22.8.6"),sQuery(id+"F0.wireOp",EDGE,"E22.8.8"),sQuery(id+"F0.wireOp",EDGE,"E22.8.9"),sQuery(id+"F0.wireOp",EDGE,"E22.8.10"),sQuery(id+"F0.wireOp",EDGE,"E22.8.11"),sQuery(id+"F0.wireOp",EDGE,"E22.9.2"),sQuery(id+"F0.wireOp",EDGE,"E22.9.3"),sQuery(id+"F0.wireOp",EDGE,"E22.9.6"),sQuery(id+"F0.wireOp",EDGE,"E22.9.8"),sQuery(id+"F0.wireOp",EDGE,"E22.9.9"),sQuery(id+"F0.wireOp",EDGE,"E22.9.10"),sQuery(id+"F0.wireOp",EDGE,"E22.9.11"),sQuery(id+"F0.wireOp",EDGE,"E22.10.2"),sQuery(id+"F0.wireOp",EDGE,"E22.10.3"),sQuery(id+"F0.wireOp",EDGE,"E22.10.6"),sQuery(id+"F0.wireOp",EDGE,"E22.10.8"),sQuery(id+"F0.wireOp",EDGE,"E22.10.9"),sQuery(id+"F0.wireOp",EDGE,"E22.10.10"),sQuery(id+"F0.wireOp",EDGE,"E22.10.11"),sQuery(id+"F0.wireOp",EDGE,"E22.11.2"),sQuery(id+"F0.wireOp",EDGE,"E22.11.3"),sQuery(id+"F0.wireOp",EDGE,"E22.11.6"),sQuery(id+"F0.wireOp",EDGE,"E22.11.8"),sQuery(id+"F0.wireOp",EDGE,"E22.11.9"),sQuery(id+"F0.wireOp",EDGE,"E22.11.10"),sQuery(id+"F0.wireOp",EDGE,"E22.11.11"),sQuery(id+"F0.wireOp",EDGE,"E22.12.2"),sQuery(id+"F0.wireOp",EDGE,"E22.12.3"),sQuery(id+"F0.wireOp",EDGE,"E22.12.6"),sQuery(id+"F0.wireOp",EDGE,"E22.12.8"),sQuery(id+"F0.wireOp",EDGE,"E22.12.9"),sQuery(id+"F0.wireOp",EDGE,"E22.12.10"),sQuery(id+"F0.wireOp",EDGE,"E22.12.11"),sQuery(id+"F0.wireOp",EDGE,"E22.13.2"),sQuery(id+"F0.wireOp",EDGE,"E22.13.3"),sQuery(id+"F0.wireOp",EDGE,"E22.13.6"),sQuery(id+"F0.wireOp",EDGE,"E22.13.8"),sQuery(id+"F0.wireOp",EDGE,"E22.13.9"),sQuery(id+"F0.wireOp",EDGE,"E22.13.10"),sQuery(id+"F0.wireOp",EDGE,"E22.13.11"),sQuery(id+"F0.wireOp",EDGE,"E22.14.2"),sQuery(id+"F0.wireOp",EDGE,"E22.14.3"),sQuery(id+"F0.wireOp",EDGE,"E22.14.6"),sQuery(id+"F0.wireOp",EDGE,"E22.14.8"),sQuery(id+"F0.wireOp",EDGE,"E22.14.9"),sQuery(id+"F0.wireOp",EDGE,"E22.14.10"),sQuery(id+"F0.wireOp",EDGE,"E22.14.11"),sQuery(id+"F0.wireOp",EDGE,"E22.15.2"),sQuery(id+"F0.wireOp",EDGE,"E22.15.3"),sQuery(id+"F0.wireOp",EDGE,"E22.15.6"),sQuery(id+"F0.wireOp",EDGE,"E22.15.8"),sQuery(id+"F0.wireOp",EDGE,"E22.15.9"),sQuery(id+"F0.wireOp",EDGE,"E22.15.10"),sQuery(id+"F0.wireOp",EDGE,"E22.15.11"),sQuery(id+"F0.wireOp",EDGE,"E22.16.2"),sQuery(id+"F0.wireOp",EDGE,"E22.16.3"),sQuery(id+"F0.wireOp",EDGE,"E22.16.6"),sQuery(id+"F0.wireOp",EDGE,"E22.16.8"),sQuery(id+"F0.wireOp",EDGE,"E22.16.9"),sQuery(id+"F0.wireOp",EDGE,"E22.16.10"),sQuery(id+"F0.wireOp",EDGE,"E22.16.11"),sQuery(id+"F0.wireOp",EDGE,"E22.17.2"),sQuery(id+"F0.wireOp",EDGE,"E22.17.3"),sQuery(id+"F0.wireOp",EDGE,"E22.17.6"),sQuery(id+"F0.wireOp",EDGE,"E22.17.8"),sQuery(id+"F0.wireOp",EDGE,"E22.17.9"),sQuery(id+"F0.wireOp",EDGE,"E22.17.10"),sQuery(id+"F0.wireOp",EDGE,"E22.17.11"),sQuery(id+"F0.wireOp",EDGE,"E22.18.2"),sQuery(id+"F0.wireOp",EDGE,"E22.18.3"),sQuery(id+"F0.wireOp",EDGE,"E22.18.6"),sQuery(id+"F0.wireOp",EDGE,"E22.18.8"),sQuery(id+"F0.wireOp",EDGE,"E22.18.9"),sQuery(id+"F0.wireOp",EDGE,"E22.18.10"),sQuery(id+"F0.wireOp",EDGE,"E22.18.11"),sQuery(id+"F0.wireOp",EDGE,"E22.19.2"),sQuery(id+"F0.wireOp",EDGE,"E22.19.3"),sQuery(id+"F0.wireOp",EDGE,"E22.19.6"),sQuery(id+"F0.wireOp",EDGE,"E22.19.8"),sQuery(id+"F0.wireOp",EDGE,"E22.19.9"),sQuery(id+"F0.wireOp",EDGE,"E22.19.10"),sQuery(id+"F0.wireOp",EDGE,"E22.19.11")])],"isStart":false});
            var sketch = newSketch(context, id + "F4", { "sketchPlane" : qUnion([Q0])});
            skCircle(sketch, "E24", {"center": v(0, 0) * mm, "radius": 1.25 * mm});
            skSolve(sketch);
        }
        {
            var Q0;
            Q0 = qSketchRegion(id + "F4", true);
            extrude(context, id + "F5", {"entities" : qUnion([Q0]), "operationType" : NewBodyOperationType.REMOVE, "oppositeDirection" : true, "depth" : 25 * mm});
        }
        {
            var Q0;
            Q0=makeQuery(id+"F3.opExtrude","CAP_FACE",FACE,{"disambiguationData":[OSD([sQuery(id+"F2.wireOp",EDGE,"E23")])],"isStart":false});
            var sketch = newSketch(context, id + "F6", { "sketchPlane" : qUnion([Q0])});
            skLineSegment(sketch, "E25", {"start": v(0, 0) * mm, "end": v(0, 16.5) * mm, "construction": true});
            skCircle(sketch, "E26", {"center": v(0, 13) * mm, "radius": 1 * mm});
            skCircle(sketch, "E27.1.0", {"center": v(-11.26, -6.5) * mm, "radius": 1 * mm});
            skCircle(sketch, "E27.2.0", {"center": v(11.26, -6.5) * mm, "radius": 1 * mm});
            skPoint(sketch, "E27.center", {"position": v(0, 0) * mm});
            skSolve(sketch);
        }
        {
            var Q0;
            Q0 = qSketchRegion(id + "F6", true);
            extrude(context, id + "F7", {"entities" : qUnion([Q0]), "operationType" : NewBodyOperationType.ADD, "depth" : 3.8 * mm});
        }
    });
